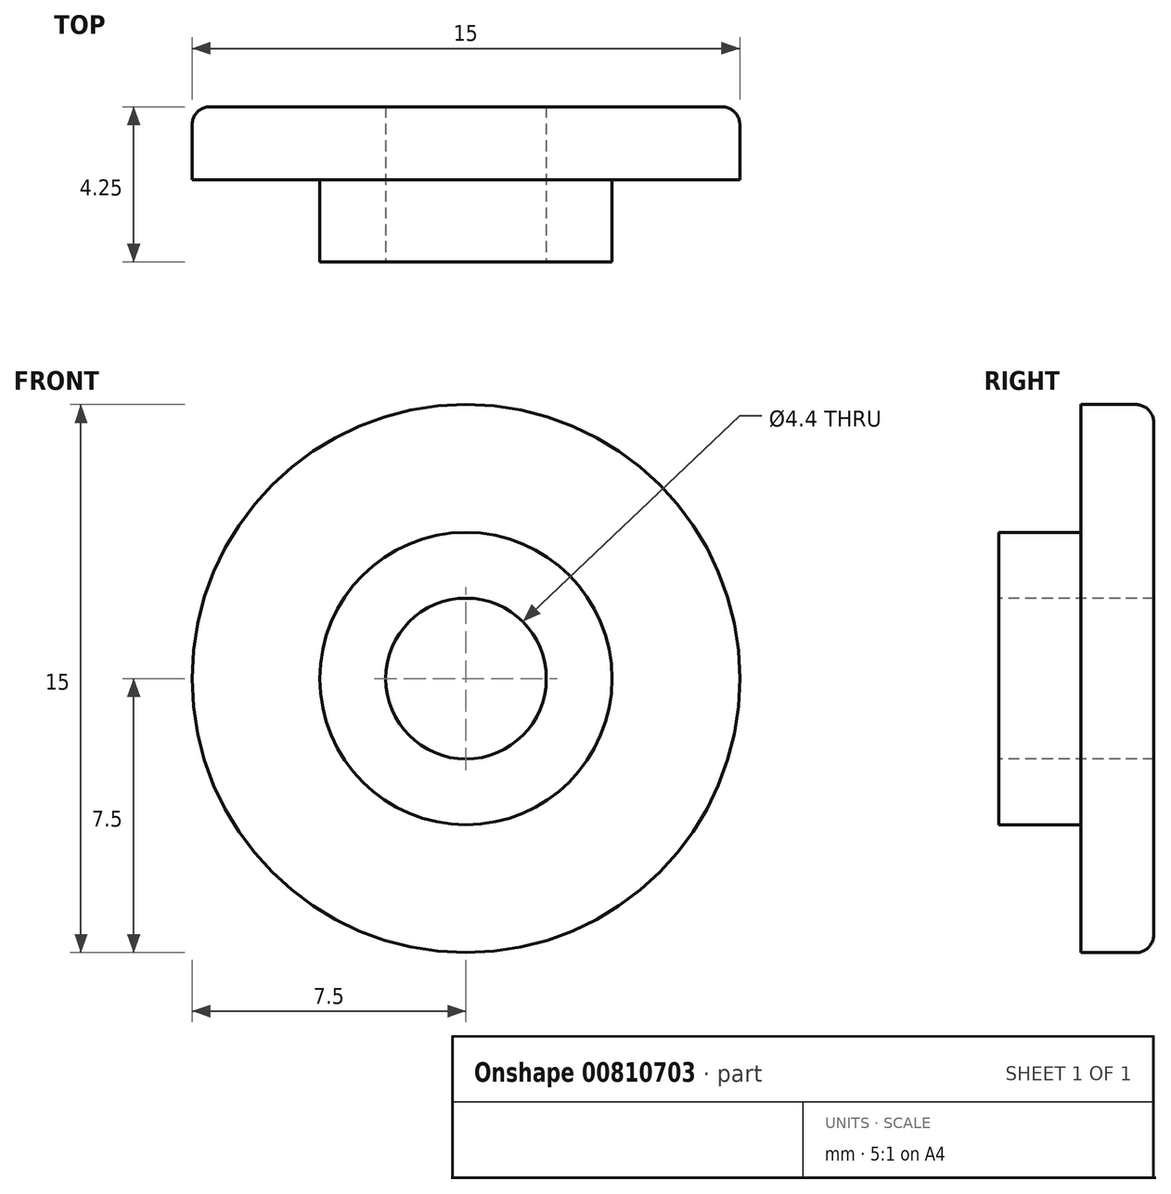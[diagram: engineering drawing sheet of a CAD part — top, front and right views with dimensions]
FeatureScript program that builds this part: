
annotation { "Feature Type Name" : "Feature", "Feature Type Description" : "" }
export const myFeature = defineFeature(function(context is Context, id is Id, definition is map)
    precondition{}
    {
        {
            var Q0;
            Q0=qCreatedBy(makeId("Front.planeOp"),FACE);
            var sketch = newSketch(context, id + "F0", { "sketchPlane" : qUnion([Q0])});
            skCircle(sketch, "E0", {"center": v(0, 0) * mm, "radius": 7.5 * mm});
            skSolve(sketch);
        }
        {
            var Q0;
            Q0=makeQuery(id+"F0.imprint","IMPRINT",FACE,{"disambiguationData":[TD([[makeQuery(id+"F0.imprint","IMPRINT",EDGE,{"derivedFrom":sQuery(id+"F0.wireOp",EDGE,"E0")}),1.0]])]});
            extrude(context, id + "F1", {"entities" : qUnion([Q0]), "depth" : 2 * mm, "offsetDistance" : 25 * mm});
        }
        {
            var Q0;
            Q0=makeQuery(id+"F1.opExtrude","CAP_FACE",FACE,{"disambiguationData":[OSD([sQuery(id+"F0.wireOp",EDGE,"E0")])],"isStart":false});
            var sketch = newSketch(context, id + "F2", { "sketchPlane" : qUnion([Q0])});
            skCircle(sketch, "E1", {"center": v(0, 0) * mm, "radius": 4 * mm});
            skSolve(sketch);
        }
        {
            var Q0;
            Q0=makeQuery(id+"F2.imprint","IMPRINT",FACE,{"disambiguationData":[TD([[makeQuery(id+"F2.imprint","IMPRINT",EDGE,{"derivedFrom":sQuery(id+"F2.wireOp",EDGE,"E1")}),1.0]])]});
            extrude(context, id + "F3", {"entities" : qUnion([Q0]), "operationType" : NewBodyOperationType.ADD, "depth" : 2.25 * mm, "offsetDistance" : 25 * mm});
        }
        {
            var Q0;
            Q0=makeQuery(id+"F3.opExtrude","CAP_FACE",FACE,{"disambiguationData":[OSD([sQuery(id+"F2.wireOp",EDGE,"E1")])],"isStart":false});
            var sketch = newSketch(context, id + "F4", { "sketchPlane" : qUnion([Q0])});
            skCircle(sketch, "E2", {"center": v(0, 0) * mm, "radius": 2.2 * mm});
            skSolve(sketch);
        }
        {
            var Q0;
            Q0=makeQuery(id+"F4.imprint","IMPRINT",FACE,{"disambiguationData":[TD([[makeQuery(id+"F4.imprint","IMPRINT",EDGE,{"derivedFrom":sQuery(id+"F4.wireOp",EDGE,"E2")}),1.0]])]});
            extrude(context, id + "F5", {"entities" : qUnion([Q0]), "operationType" : NewBodyOperationType.REMOVE, "endBound" : BoundingType.THROUGH_ALL, "oppositeDirection" : true, "depth" : 25 * mm, "offsetDistance" : 25 * mm});
        }
        {
            var Q0;
            Q0=makeQuery(id+"F1.opExtrude","CAP_EDGE",EDGE,{"disambiguationData":[OSD([sQuery(id+"F0.wireOp",EDGE,"E0")])],"isStart":true});
            fillet(context, id + "F6", {"entities" : qUnion([Q0]), "radius" : .5 * mm, "tangentPropagation" : true, "allowEdgeOverflow" : false});
        }
    });
